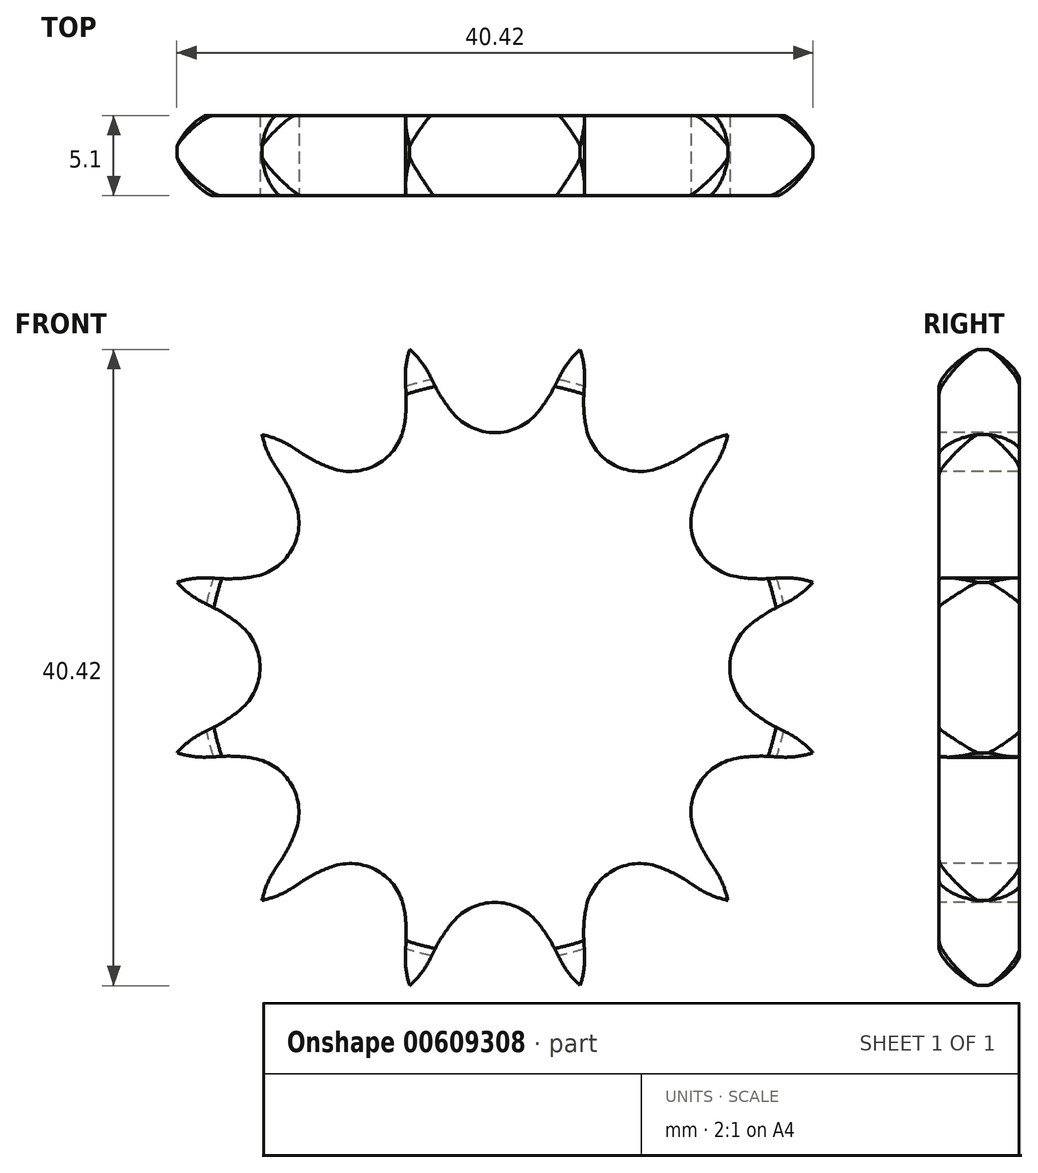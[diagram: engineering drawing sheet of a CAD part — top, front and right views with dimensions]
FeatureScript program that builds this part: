
annotation { "Feature Type Name" : "Feature", "Feature Type Description" : "" }
export const myFeature = defineFeature(function(context is Context, id is Id, definition is map)
    precondition{}
    {
        {
            var Q0;
            Q0=qCreatedBy(makeId("Right.planeOp"),FACE);
            var sketch = newSketch(context, id + "F0", { "sketchPlane" : qUnion([Q0])});
            skLineSegment(sketch, "E0", {"start": v(0, 0) * mm, "end": v(5.1, 0) * mm, "construction": true});
            skLineSegment(sketch, "E1", {"start": v(0, 21) * mm, "end": v(5.1, 21) * mm});
            skLineSegment(sketch, "E2", {"start": v(5.1, 21) * mm, "end": v(5.1, 15) * mm});
            skLineSegment(sketch, "E3", {"start": v(5.1, 15) * mm, "end": v(5.1, 15) * mm});
            skLineSegment(sketch, "E4", {"start": v(5.1, 15) * mm, "end": v(5.1, 0) * mm});
            skLineSegment(sketch, "E5", {"start": v(0, 0) * mm, "end": v(0, 21) * mm});
            skLineSegment(sketch, "E6.0.MirrorCS", {"start": v(0, -21) * mm, "end": v(5.1, -21) * mm});
            skLineSegment(sketch, "E6.1.MirrorCS", {"start": v(5.1, -21) * mm, "end": v(5.1, -15) * mm});
            skLineSegment(sketch, "E6.3.MirrorCS", {"start": v(5.1, -15) * mm, "end": v(5.1, 0) * mm});
            skLineSegment(sketch, "E6.4.MirrorCS", {"start": v(5.1, -15) * mm, "end": v(5.1, -15) * mm});
            skLineSegment(sketch, "E6.5.MirrorCS", {"start": v(0, 0) * mm, "end": v(0, -21) * mm});
            skLineSegment(sketch, "E7", {"start": v(0, 0) * mm, "end": v(5.1, 0) * mm});
            skSolve(sketch);
        }
        {
            var Q0;
            Q0=makeQuery(id+"F0.imprint","IMPRINT",FACE,{"disambiguationData":[TD([[makeQuery(id+"F0.imprint","IMPRINT",EDGE,{"derivedFrom":sQuery(id+"F0.wireOp",EDGE,"E1")}),-1.0]])]});
            var Q1;
            Q1=sQuery(id+"F0.wireOp",EDGE,"E0");
            revolve(context, id + "F1", {"entities" : qUnion([Q0]), "axis" : qUnion([Q1]), "revolveType" : RevolveType.FULL});
        }
        {
            var Q0;
            Q0=makeQuery(id+"F1.opRevolve","SWEPT_EDGE",EDGE,{"disambiguationData":[OSD([sQuery(id+"F0.wireOp",EDGE,"E1"),sQuery(id+"F0.wireOp",EDGE,"E5")])]});
            fillet(context, id + "F2", {"entities" : qUnion([Q0]), "radius" : 2.75 * mm, "tangentPropagation" : true, "rho" : 0.2, "crossSection" : FilletCrossSection.CONIC, "allowEdgeOverflow" : false});
        }
        {
            var Q0;
            Q0=makeQuery(id+"F1.opRevolve","SWEPT_EDGE",EDGE,{"disambiguationData":[OSD([sQuery(id+"F0.wireOp",EDGE,"E1"),sQuery(id+"F0.wireOp",EDGE,"E2")])]});
            fillet(context, id + "F3", {"entities" : qUnion([Q0]), "radius" : 2.25 * mm, "tangentPropagation" : true, "rho" : 0.2, "crossSection" : FilletCrossSection.CONIC, "allowEdgeOverflow" : false});
        }
        {
            var Q0;
            Q0=qCreatedBy(makeId("Front.planeOp"),FACE);
            var sketch = newSketch(context, id + "F4", { "sketchPlane" : qUnion([Q0])});
            skPoint(sketch, "E8.0", {"position": v(0, 0) * mm});
            skArc(sketch, "E9", {"start": v(2.67, 16.16) * mm, "mid": v(0, 21.88) * mm, "end": v(-2.67, 16.16) * mm, "construction": true});
            skLineSegment(sketch, "E10", {"start": v(0, 0) * mm, "end": v(7.32, 0) * mm, "construction": true});
            skArc(sketch, "E11", {"start": v(-2.67, 16.16) * mm, "mid": v(11.7, 26.86) * mm, "end": v(-3.81, 17.9) * mm, "construction": true});
            skLineSegment(sketch, "E12", {"start": v(4.9, 0.57) * mm, "end": v(-4.12, 18.5) * mm, "construction": true});
            skArc(sketch, "E13", {"start": v(-5.41, 20.2) * mm, "mid": v(-13.86, 12.42) * mm, "end": v(-4.12, 18.5) * mm, "construction": true});
            skLineSegment(sketch, "E14", {"start": v(0, 0) * mm, "end": v(-5.41, 20.2) * mm, "construction": true});
            skLineSegment(sketch, "E15", {"start": v(4.2, 21.93) * mm, "end": v(-3.81, 17.9) * mm, "construction": true});
            skLineSegment(sketch, "E16", {"start": v(0, 18.4) * mm, "end": v(4.2, 21.93) * mm, "construction": true});
            skLineSegment(sketch, "E17", {"start": v(0, 18.4) * mm, "end": v(72.06, 18.4) * mm, "construction": true});
            skLineSegment(sketch, "E18", {"start": v(0, 0) * mm, "end": v(0, 18.4) * mm, "construction": true});
            skCircle(sketch, "E19", {"center": v(0, 0) * mm, "radius": 18.4 * mm, "construction": true});
            skArc(sketch, "E20", {"start": v(-2.67, 16.16) * mm, "mid": v(0, 14.92) * mm, "end": v(2.67, 16.16) * mm});
            skArc(sketch, "E21.0.MirrorCS", {"start": v(4.12, 18.5) * mm, "mid": v(4.69, 19.42) * mm, "end": v(5.41, 20.2) * mm});
            skLineSegment(sketch, "E22.0.MirrorCS", {"start": v(3.81, 17.9) * mm, "end": v(4.12, 18.5) * mm});
            skArc(sketch, "E23.0.MirrorCS", {"start": v(3.81, 17.9) * mm, "mid": v(3.3, 17) * mm, "end": v(2.67, 16.16) * mm});
            skArc(sketch, "E24", {"start": v(-3.81, 17.9) * mm, "mid": v(-3.3, 17) * mm, "end": v(-2.67, 16.16) * mm});
            skArc(sketch, "E25", {"start": v(-4.12, 18.5) * mm, "mid": v(-4.69, 19.42) * mm, "end": v(-5.41, 20.2) * mm});
            skLineSegment(sketch, "E26", {"start": v(-3.81, 17.9) * mm, "end": v(-4.12, 18.5) * mm});
            skArc(sketch, "E27.1.0", {"start": v(-12.82, 13.97) * mm, "mid": v(-13.77, 14.47) * mm, "end": v(-14.8, 14.8) * mm});
            skLineSegment(sketch, "E27.1.1", {"start": v(-12.25, 13.6) * mm, "end": v(-12.82, 13.97) * mm});
            skArc(sketch, "E27.1.2", {"start": v(-12.25, 13.6) * mm, "mid": v(-11.35, 13.07) * mm, "end": v(-10.4, 12.66) * mm});
            skArc(sketch, "E27.1.3", {"start": v(-5.65, 17.4) * mm, "mid": v(-5.65, 16.37) * mm, "end": v(-5.77, 15.33) * mm});
            skLineSegment(sketch, "E27.1.4", {"start": v(-5.65, 17.4) * mm, "end": v(-5.69, 18.08) * mm});
            skArc(sketch, "E27.1.5", {"start": v(-5.69, 18.08) * mm, "mid": v(-5.65, 19.16) * mm, "end": v(-5.41, 20.2) * mm});
            skArc(sketch, "E27.1.6", {"start": v(-10.4, 12.66) * mm, "mid": v(-7.46, 12.92) * mm, "end": v(-5.77, 15.33) * mm});
            skArc(sketch, "E27.2.0", {"start": v(-18.08, 5.69) * mm, "mid": v(-19.16, 5.65) * mm, "end": v(-20.2, 5.41) * mm});
            skLineSegment(sketch, "E27.2.1", {"start": v(-17.4, 5.65) * mm, "end": v(-18.08, 5.69) * mm});
            skArc(sketch, "E27.2.2", {"start": v(-17.4, 5.65) * mm, "mid": v(-16.37, 5.65) * mm, "end": v(-15.33, 5.77) * mm});
            skArc(sketch, "E27.2.3", {"start": v(-13.6, 12.25) * mm, "mid": v(-13.07, 11.35) * mm, "end": v(-12.66, 10.4) * mm});
            skLineSegment(sketch, "E27.2.4", {"start": v(-13.6, 12.25) * mm, "end": v(-13.97, 12.82) * mm});
            skArc(sketch, "E27.2.5", {"start": v(-13.97, 12.82) * mm, "mid": v(-14.47, 13.77) * mm, "end": v(-14.8, 14.8) * mm});
            skArc(sketch, "E27.2.6", {"start": v(-15.33, 5.77) * mm, "mid": v(-12.92, 7.46) * mm, "end": v(-12.66, 10.4) * mm});
            skArc(sketch, "E27.3.0", {"start": v(-18.5, -4.12) * mm, "mid": v(-19.42, -4.69) * mm, "end": v(-20.2, -5.41) * mm});
            skLineSegment(sketch, "E27.3.1", {"start": v(-17.9, -3.81) * mm, "end": v(-18.5, -4.12) * mm});
            skArc(sketch, "E27.3.2", {"start": v(-17.9, -3.81) * mm, "mid": v(-17, -3.3) * mm, "end": v(-16.16, -2.67) * mm});
            skArc(sketch, "E27.3.3", {"start": v(-17.9, 3.81) * mm, "mid": v(-17, 3.3) * mm, "end": v(-16.16, 2.67) * mm});
            skLineSegment(sketch, "E27.3.4", {"start": v(-17.9, 3.81) * mm, "end": v(-18.5, 4.12) * mm});
            skArc(sketch, "E27.3.5", {"start": v(-18.5, 4.12) * mm, "mid": v(-19.42, 4.69) * mm, "end": v(-20.2, 5.41) * mm});
            skArc(sketch, "E27.3.6", {"start": v(-16.16, -2.67) * mm, "mid": v(-14.92, 0) * mm, "end": v(-16.16, 2.67) * mm});
            skArc(sketch, "E27.4.0", {"start": v(-13.97, -12.82) * mm, "mid": v(-14.47, -13.77) * mm, "end": v(-14.8, -14.8) * mm});
            skLineSegment(sketch, "E27.4.1", {"start": v(-13.6, -12.25) * mm, "end": v(-13.97, -12.82) * mm});
            skArc(sketch, "E27.4.2", {"start": v(-13.6, -12.25) * mm, "mid": v(-13.07, -11.35) * mm, "end": v(-12.66, -10.4) * mm});
            skArc(sketch, "E27.4.3", {"start": v(-17.4, -5.65) * mm, "mid": v(-16.37, -5.65) * mm, "end": v(-15.33, -5.77) * mm});
            skLineSegment(sketch, "E27.4.4", {"start": v(-17.4, -5.65) * mm, "end": v(-18.08, -5.69) * mm});
            skArc(sketch, "E27.4.5", {"start": v(-18.08, -5.69) * mm, "mid": v(-19.16, -5.65) * mm, "end": v(-20.2, -5.41) * mm});
            skArc(sketch, "E27.4.6", {"start": v(-12.66, -10.4) * mm, "mid": v(-12.92, -7.46) * mm, "end": v(-15.33, -5.77) * mm});
            skArc(sketch, "E27.5.0", {"start": v(-5.69, -18.08) * mm, "mid": v(-5.65, -19.16) * mm, "end": v(-5.41, -20.2) * mm});
            skLineSegment(sketch, "E27.5.1", {"start": v(-5.65, -17.4) * mm, "end": v(-5.69, -18.08) * mm});
            skArc(sketch, "E27.5.2", {"start": v(-5.65, -17.4) * mm, "mid": v(-5.65, -16.37) * mm, "end": v(-5.77, -15.33) * mm});
            skArc(sketch, "E27.5.3", {"start": v(-12.25, -13.6) * mm, "mid": v(-11.35, -13.07) * mm, "end": v(-10.4, -12.66) * mm});
            skLineSegment(sketch, "E27.5.4", {"start": v(-12.25, -13.6) * mm, "end": v(-12.82, -13.97) * mm});
            skArc(sketch, "E27.5.5", {"start": v(-12.82, -13.97) * mm, "mid": v(-13.77, -14.47) * mm, "end": v(-14.8, -14.8) * mm});
            skArc(sketch, "E27.5.6", {"start": v(-5.77, -15.33) * mm, "mid": v(-7.46, -12.92) * mm, "end": v(-10.4, -12.66) * mm});
            skArc(sketch, "E27.6.0", {"start": v(4.12, -18.5) * mm, "mid": v(4.69, -19.42) * mm, "end": v(5.41, -20.2) * mm});
            skLineSegment(sketch, "E27.6.1", {"start": v(3.81, -17.9) * mm, "end": v(4.12, -18.5) * mm});
            skArc(sketch, "E27.6.2", {"start": v(3.81, -17.9) * mm, "mid": v(3.3, -17) * mm, "end": v(2.67, -16.16) * mm});
            skArc(sketch, "E27.6.3", {"start": v(-3.81, -17.9) * mm, "mid": v(-3.3, -17) * mm, "end": v(-2.67, -16.16) * mm});
            skLineSegment(sketch, "E27.6.4", {"start": v(-3.81, -17.9) * mm, "end": v(-4.12, -18.5) * mm});
            skArc(sketch, "E27.6.5", {"start": v(-4.12, -18.5) * mm, "mid": v(-4.69, -19.42) * mm, "end": v(-5.41, -20.2) * mm});
            skArc(sketch, "E27.6.6", {"start": v(2.67, -16.16) * mm, "mid": v(0, -14.92) * mm, "end": v(-2.67, -16.16) * mm});
            skArc(sketch, "E27.7.0", {"start": v(12.82, -13.97) * mm, "mid": v(13.77, -14.47) * mm, "end": v(14.8, -14.8) * mm});
            skLineSegment(sketch, "E27.7.1", {"start": v(12.25, -13.6) * mm, "end": v(12.82, -13.97) * mm});
            skArc(sketch, "E27.7.2", {"start": v(12.25, -13.6) * mm, "mid": v(11.35, -13.07) * mm, "end": v(10.4, -12.66) * mm});
            skArc(sketch, "E27.7.3", {"start": v(5.65, -17.4) * mm, "mid": v(5.65, -16.37) * mm, "end": v(5.77, -15.33) * mm});
            skLineSegment(sketch, "E27.7.4", {"start": v(5.65, -17.4) * mm, "end": v(5.69, -18.08) * mm});
            skArc(sketch, "E27.7.5", {"start": v(5.69, -18.08) * mm, "mid": v(5.65, -19.16) * mm, "end": v(5.41, -20.2) * mm});
            skArc(sketch, "E27.7.6", {"start": v(10.4, -12.66) * mm, "mid": v(7.46, -12.92) * mm, "end": v(5.77, -15.33) * mm});
            skArc(sketch, "E27.8.0", {"start": v(18.08, -5.69) * mm, "mid": v(19.16, -5.65) * mm, "end": v(20.2, -5.41) * mm});
            skLineSegment(sketch, "E27.8.1", {"start": v(17.4, -5.65) * mm, "end": v(18.08, -5.69) * mm});
            skArc(sketch, "E27.8.2", {"start": v(17.4, -5.65) * mm, "mid": v(16.37, -5.65) * mm, "end": v(15.33, -5.77) * mm});
            skArc(sketch, "E27.8.3", {"start": v(13.6, -12.25) * mm, "mid": v(13.07, -11.35) * mm, "end": v(12.66, -10.4) * mm});
            skLineSegment(sketch, "E27.8.4", {"start": v(13.6, -12.25) * mm, "end": v(13.97, -12.82) * mm});
            skArc(sketch, "E27.8.5", {"start": v(13.97, -12.82) * mm, "mid": v(14.47, -13.77) * mm, "end": v(14.8, -14.8) * mm});
            skArc(sketch, "E27.8.6", {"start": v(15.33, -5.77) * mm, "mid": v(12.92, -7.46) * mm, "end": v(12.66, -10.4) * mm});
            skArc(sketch, "E27.9.0", {"start": v(18.5, 4.12) * mm, "mid": v(19.42, 4.69) * mm, "end": v(20.2, 5.41) * mm});
            skLineSegment(sketch, "E27.9.1", {"start": v(17.9, 3.81) * mm, "end": v(18.5, 4.12) * mm});
            skArc(sketch, "E27.9.2", {"start": v(17.9, 3.81) * mm, "mid": v(17, 3.3) * mm, "end": v(16.16, 2.67) * mm});
            skArc(sketch, "E27.9.3", {"start": v(17.9, -3.81) * mm, "mid": v(17, -3.3) * mm, "end": v(16.16, -2.67) * mm});
            skLineSegment(sketch, "E27.9.4", {"start": v(17.9, -3.81) * mm, "end": v(18.5, -4.12) * mm});
            skArc(sketch, "E27.9.5", {"start": v(18.5, -4.12) * mm, "mid": v(19.42, -4.69) * mm, "end": v(20.2, -5.41) * mm});
            skArc(sketch, "E27.9.6", {"start": v(16.16, 2.67) * mm, "mid": v(14.92, 0) * mm, "end": v(16.16, -2.67) * mm});
            skArc(sketch, "E27.10.0", {"start": v(13.97, 12.82) * mm, "mid": v(14.47, 13.77) * mm, "end": v(14.8, 14.8) * mm});
            skLineSegment(sketch, "E27.10.1", {"start": v(13.6, 12.25) * mm, "end": v(13.97, 12.82) * mm});
            skArc(sketch, "E27.10.2", {"start": v(13.6, 12.25) * mm, "mid": v(13.07, 11.35) * mm, "end": v(12.66, 10.4) * mm});
            skArc(sketch, "E27.10.3", {"start": v(17.4, 5.65) * mm, "mid": v(16.37, 5.65) * mm, "end": v(15.33, 5.77) * mm});
            skLineSegment(sketch, "E27.10.4", {"start": v(17.4, 5.65) * mm, "end": v(18.08, 5.69) * mm});
            skArc(sketch, "E27.10.5", {"start": v(18.08, 5.69) * mm, "mid": v(19.16, 5.65) * mm, "end": v(20.2, 5.41) * mm});
            skArc(sketch, "E27.10.6", {"start": v(12.66, 10.4) * mm, "mid": v(12.92, 7.46) * mm, "end": v(15.33, 5.77) * mm});
            skArc(sketch, "E27.11.0", {"start": v(5.69, 18.08) * mm, "mid": v(5.65, 19.16) * mm, "end": v(5.41, 20.2) * mm});
            skLineSegment(sketch, "E27.11.1", {"start": v(5.65, 17.4) * mm, "end": v(5.69, 18.08) * mm});
            skArc(sketch, "E27.11.2", {"start": v(5.65, 17.4) * mm, "mid": v(5.65, 16.37) * mm, "end": v(5.77, 15.33) * mm});
            skArc(sketch, "E27.11.3", {"start": v(12.25, 13.6) * mm, "mid": v(11.35, 13.07) * mm, "end": v(10.4, 12.66) * mm});
            skLineSegment(sketch, "E27.11.4", {"start": v(12.25, 13.6) * mm, "end": v(12.82, 13.97) * mm});
            skArc(sketch, "E27.11.5", {"start": v(12.82, 13.97) * mm, "mid": v(13.77, 14.47) * mm, "end": v(14.8, 14.8) * mm});
            skArc(sketch, "E27.11.6", {"start": v(5.77, 15.33) * mm, "mid": v(7.46, 12.92) * mm, "end": v(10.4, 12.66) * mm});
            skSolve(sketch);
        }
        {
            var Q0;
            Q0=qSketchRegion(id+"F4",true);
            extrude(context, id + "F5", {"entities" : qUnion([Q0]), "operationType" : NewBodyOperationType.INTERSECT, "endBound" : BoundingType.THROUGH_ALL, "oppositeDirection" : true, "depth" : 25.4 * mm});
        }
    });
